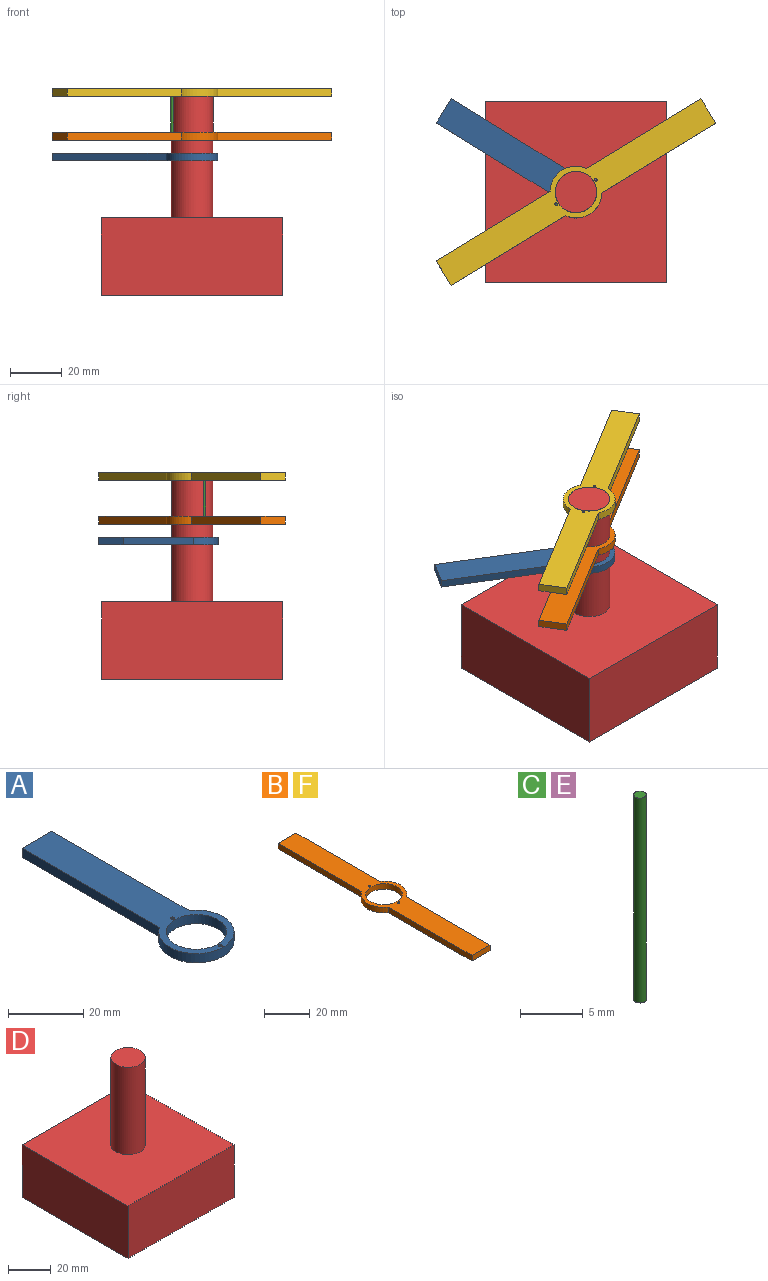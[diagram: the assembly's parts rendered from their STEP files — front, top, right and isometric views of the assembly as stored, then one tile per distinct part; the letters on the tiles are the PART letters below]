
ASSEMBLY  parts=6 mates=6
PART A: 9 faces, bbox 20x70x3 mm
  f0: cylinder r=10mm len=20mm, axis (0,0,-1), area 153.2mm2, adj f1,f3,f4,f5
  f1: plane 51.68x3mm, normal (-1,0,0), area 155mm2, adj f0,f2,f4,f5
  f2: plane 11.1x3mm, normal (0,1,0), area 33.3mm2, adj f1,f3,f4,f5
  f3: plane 51.68x3mm, normal (1,0,0), area 155mm2, adj f0,f2,f4,f5
  f4: plane 70x20mm, normal (0,0,1), area 672.7mm2, adj f0,f1,f2,f3,f6,f7,f8
  f5: plane 70x20mm, normal (0,0,-1), area 672.7mm2, adj f0,f1,f2,f3,f6,f7,f8
  f6: cylinder r=8mm len=16mm, axis (0,0,-1), area 150.8mm2, adj f4,f5
  f7: cylinder r=0.5mm len=3mm, axis (0,0,1), area 9.4mm2, adj f4,f5
  f8: cylinder r=0.5mm len=3mm, axis (0,0,1), area 9.4mm2, adj f4,f5
PART B: 13 faces, bbox 20x120x3 mm
  f0: cylinder r=10mm len=16.63mm, axis (0,0,-1), area 58.9mm2, adj f4,f5,f6,f12
  f1: cylinder r=10mm len=16.63mm, axis (0,0,-1), area 58.9mm2, adj f2,f5,f6,f10
  f2: plane 51.68x3mm, normal (-1,0,0), area 155mm2, adj f1,f3,f5,f6
  f3: plane 11.1x3mm, normal (0,-1,0), area 33.3mm2, adj f2,f4,f5,f6
  f4: plane 51.68x3mm, normal (1,0,0), area 155mm2, adj f0,f3,f5,f6
  f5: plane 120x20mm, normal (0,0,1), area 1233.9mm2, adj f0,f1,f2,f3,f4,f7,f8,f9
  f6: plane 120x20mm, normal (0,0,-1), area 1233.9mm2, adj f0,f1,f2,f3,f4,f7,f8,f9
  f7: cylinder r=8mm len=16mm, axis (0,0,-1), area 150.8mm2, adj f5,f6
  f8: cylinder r=0.5mm len=3mm, axis (0,0,1), area 9.4mm2, adj f5,f6
  f9: cylinder r=0.5mm len=3mm, axis (0,0,1), area 9.4mm2, adj f5,f6
  f10: plane 51.68x3mm, normal (-1,0,0), area 155mm2, adj f1,f5,f6,f11
  f11: plane 11.1x3mm, normal (0,1,0), area 33.3mm2, adj f5,f6,f10,f12
  f12: plane 51.68x3mm, normal (1,0,0), area 155mm2, adj f0,f5,f6,f11
PART C: 3 faces, bbox 1x1x20 mm
  f0: cylinder r=0.5mm len=20mm, axis (0,0,-1), area 62.8mm2, adj f1,f2
  f1: plane 1x1mm, normal (0,0,1), area 0.8mm2, adj f0
  f2: plane 1x1mm, normal (0,0,-1), area 0.8mm2, adj f0
PART D: 8 faces, bbox 70x70x80 mm
  f0: cylinder r=8mm len=50mm, axis (0,0,-1), area 2513.3mm2, adj f1,f6
  f1: plane 16x16mm, normal (0,0,1), area 201.1mm2, adj f0
  f2: plane 70x30mm, normal (1,0,0), area 2100mm2, adj f3,f5,f6,f7
  f3: plane 70x30mm, normal (0,1,0), area 2100mm2, adj f2,f4,f6,f7
  f4: plane 70x30mm, normal (-1,0,0), area 2100mm2, adj f3,f5,f6,f7
  f5: plane 70x30mm, normal (0,-1,0), area 2100mm2, adj f2,f4,f6,f7
  f6: plane 70x70mm, normal (0,0,1), area 4698.9mm2, adj f0,f2,f3,f4,f5
  f7: plane 70x70mm, normal (0,0,-1), area 4900mm2, adj f2,f3,f4,f5
PART E: same geometry as C
PART F: same geometry as B
PLACE A rot(axis=(0,0,1),58.4deg) t=(-11.32,-20.43,-3.51)mm
PLACE B rot(axis=(0,0,1),121.4deg) t=(-11.32,-20.43,-11.91)mm
PLACE C rot(axis=(0,0,-1),58.6deg) t=(-26.68,-29.82,5.59)mm
PLACE D t=(-11.32,-20.43,-5.51)mm fixed
PLACE E rot(axis=(0,0,-1),58.6deg) t=(-11.32,-20.43,5.59)mm
PLACE F rot(axis=(0,0,-1),58.6deg) t=(-11.32,-20.43,5.09)mm
MATE fastened C.f0 <-> B.f8  axis (0,0,-1) through (-19,-25.13,54.49)mm
MATE revolute F.f7 <-> D.f0  axis (0,0,1) through (-11.32,-20.43,74.49)mm
MATE fastened F.f8 <-> E.f0  axis (0,0,1) through (-3.64,-15.74,74.49)mm
MATE fastened F.f9 <-> C.f0  axis (0,0,1) through (-19,-25.13,74.49)mm
MATE planar D.f0 <-> F.f7  axis (0,0,1) through (-11.32,-20.43,74.49)mm
MATE cylindrical A.f6 <-> D.f0  axis (0,0,1) through (-11.32,-20.43,49.49)mm
